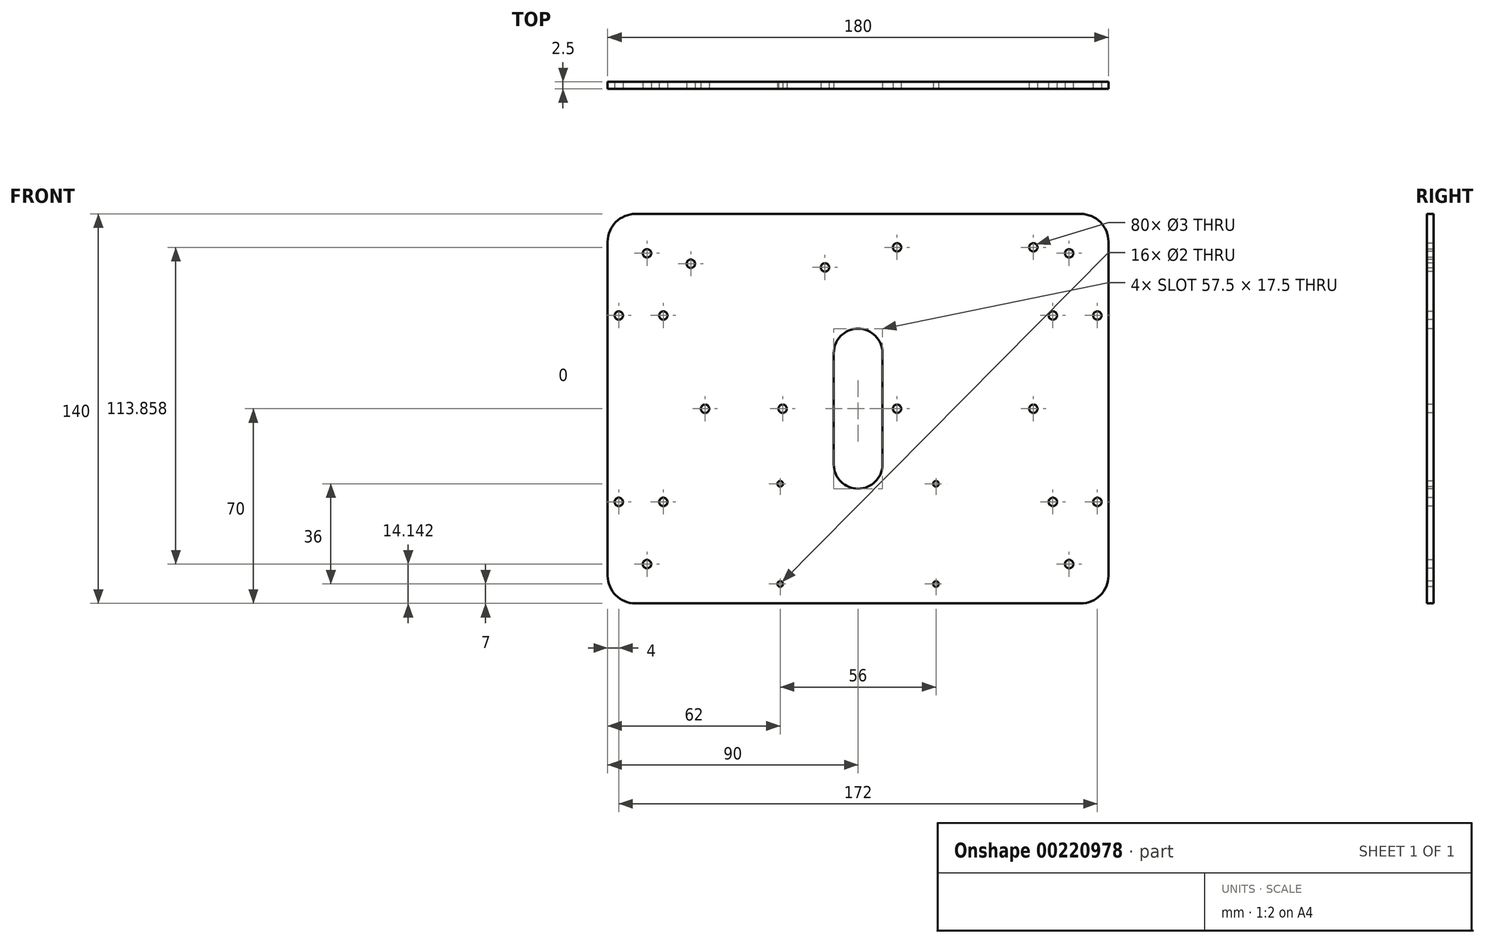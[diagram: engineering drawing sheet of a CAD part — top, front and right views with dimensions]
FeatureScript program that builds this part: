
annotation { "Feature Type Name" : "Feature", "Feature Type Description" : "" }
export const myFeature = defineFeature(function(context is Context, id is Id, definition is map)
    precondition{}
    {
        {
            var Q0;
            Q0=qCreatedBy(makeId("Front.planeOp"),FACE);
            var sketch = newSketch(context, id + "F0", { "sketchPlane" : qUnion([Q0])});
            skLineSegment(sketch, "E0.bottom", {"start": v(90, 70) * mm, "end": v(-90, 70) * mm});
            skLineSegment(sketch, "E0.top", {"start": v(90, -70) * mm, "end": v(-90, -70) * mm});
            skLineSegment(sketch, "E0.left", {"start": v(90, 70) * mm, "end": v(90, -70) * mm});
            skLineSegment(sketch, "E0.right", {"start": v(-90, 70) * mm, "end": v(-90, -70) * mm});
            skPoint(sketch, "E0.middle", {"position": v(0, 0) * mm});
            skSolve(sketch);
        }
        {
            var Q0;
            Q0 = qSketchRegion(id + "F0", true);
            extrude(context, id + "F1", {"entities" : qUnion([Q0]), "depth" : 2.5 * mm});
        }
        {
            var Q0;
            Q0=makeQuery(id+"F1.opExtrude","CAP_FACE",FACE,{"disambiguationData":[OSD([sQuery(id+"F0.wireOp",EDGE,"E0.bottom"),sQuery(id+"F0.wireOp",EDGE,"E0.top"),sQuery(id+"F0.wireOp",EDGE,"E0.left"),sQuery(id+"F0.wireOp",EDGE,"E0.right")])],"isStart":false});
            var sketch = newSketch(context, id + "F2", { "sketchPlane" : qUnion([Q0])});
            skCircle(sketch, "E1", {"center": v(75.86, 55.86) * mm, "radius": 1.5 * mm});
            skCircle(sketch, "E2.MirrorC", {"center": v(-75.86, 55.86) * mm, "radius": 1.5 * mm});
            skCircle(sketch, "E3.MirrorC", {"center": v(75.86, -55.86) * mm, "radius": 1.5 * mm});
            skCircle(sketch, "E4.MirrorC", {"center": v(-75.86, -55.86) * mm, "radius": 1.5 * mm});
            skLineSegment(sketch, "E5", {"start": v(-8.75, 0) * mm, "end": v(-8.75, 20) * mm});
            skLineSegment(sketch, "E6", {"start": v(8.75, 0) * mm, "end": v(8.75, 20) * mm});
            skArc(sketch, "E7", {"start": v(-8.75, 20) * mm, "mid": v(0, 28.75) * mm, "end": v(8.75, 20) * mm});
            skLineSegment(sketch, "E8.MirrorCS", {"start": v(-8.75, 0) * mm, "end": v(-8.75, -20) * mm});
            skArc(sketch, "E9.MirrorCS", {"start": v(-8.75, -20) * mm, "mid": v(0, -28.75) * mm, "end": v(8.75, -20) * mm});
            skLineSegment(sketch, "E10.MirrorCS", {"start": v(8.75, 0) * mm, "end": v(8.75, -20) * mm});
            skLineSegment(sketch, "E11", {"start": v(-90, 0) * mm, "end": v(-55, 0) * mm});
            skCircle(sketch, "E12", {"center": v(-55, 0) * mm, "radius": 1.5 * mm});
            skLineSegment(sketch, "E13", {"start": v(-55, 0) * mm, "end": v(-55, 52.1) * mm});
            skLineSegment(sketch, "E14", {"start": v(-55, 52.1) * mm, "end": v(-60.1, 52.1) * mm});
            skCircle(sketch, "E15", {"center": v(-60.1, 52.1) * mm, "radius": 1.5 * mm});
            skLineSegment(sketch, "E16", {"start": v(-55, 52.1) * mm, "end": v(-11.9, 52.1) * mm});
            skLineSegment(sketch, "E17", {"start": v(-11.9, 52.1) * mm, "end": v(-11.9, 50.8) * mm});
            skCircle(sketch, "E18", {"center": v(-11.9, 50.8) * mm, "radius": 1.5 * mm});
            skLineSegment(sketch, "E19", {"start": v(90, 0) * mm, "end": v(63, 0) * mm});
            skPoint(sketch, "E19.endSnap0", {"position": v(90, 0) * mm});
            skCircle(sketch, "E20", {"center": v(63, 0) * mm, "radius": 1.5 * mm});
            skLineSegment(sketch, "E21", {"start": v(63, 0) * mm, "end": v(63, 58) * mm});
            skLineSegment(sketch, "E22", {"start": v(63, 58) * mm, "end": v(14, 58) * mm});
            skLineSegment(sketch, "E23", {"start": v(14, 58) * mm, "end": v(14, 0) * mm});
            skCircle(sketch, "E24", {"center": v(14, 0) * mm, "radius": 1.5 * mm});
            skCircle(sketch, "E25", {"center": v(14, 58) * mm, "radius": 1.5 * mm});
            skCircle(sketch, "E26", {"center": v(63, 58) * mm, "radius": 1.5 * mm});
            skLineSegment(sketch, "E27", {"start": v(-55, 0) * mm, "end": v(-27.1, 0) * mm});
            skCircle(sketch, "E28", {"center": v(-27.1, 0) * mm, "radius": 1.5 * mm});
            skLineSegment(sketch, "E29.bottom", {"start": v(30, -65) * mm, "end": v(-30, -65) * mm});
            skPoint(sketch, "E29.middle", {"position": v(0, -45) * mm});
            skLineSegment(sketch, "E30", {"start": v(0, -70) * mm, "end": v(0, -65) * mm});
            skLineSegment(sketch, "E31", {"start": v(-30, -65) * mm, "end": v(-28, -65) * mm});
            skLineSegment(sketch, "E32", {"start": v(-28, -65) * mm, "end": v(-28, -63) * mm});
            skLineSegment(sketch, "E33", {"start": v(-28, -63) * mm, "end": v(-28, -27) * mm});
            skLineSegment(sketch, "E34", {"start": v(-28, -27) * mm, "end": v(28, -27) * mm});
            skLineSegment(sketch, "E35", {"start": v(28, -27) * mm, "end": v(28, -63) * mm});
            skCircle(sketch, "E36", {"center": v(-28, -27) * mm, "radius": 1 * mm});
            skCircle(sketch, "E37", {"center": v(28, -27) * mm, "radius": 1 * mm});
            skCircle(sketch, "E38", {"center": v(-28, -63) * mm, "radius": 1 * mm});
            skCircle(sketch, "E39", {"center": v(28, -63) * mm, "radius": 1 * mm});
            skLineSegment(sketch, "E40", {"start": v(90, 0) * mm, "end": v(78, 0) * mm});
            skLineSegment(sketch, "E41", {"start": v(78, 0) * mm, "end": v(78, 33.5) * mm});
            skLineSegment(sketch, "E42", {"start": v(78, 0) * mm, "end": v(78, -33.5) * mm});
            skLineSegment(sketch, "E43", {"start": v(78, -33.5) * mm, "end": v(70, -33.5) * mm});
            skLineSegment(sketch, "E44", {"start": v(78, -33.5) * mm, "end": v(86, -33.5) * mm});
            skLineSegment(sketch, "E45", {"start": v(78, 33.5) * mm, "end": v(86, 33.5) * mm});
            skLineSegment(sketch, "E46", {"start": v(78, 33.5) * mm, "end": v(70, 33.5) * mm});
            skLineSegment(sketch, "E47", {"start": v(-90, 0) * mm, "end": v(-78, 0) * mm});
            skLineSegment(sketch, "E48", {"start": v(-78, 0) * mm, "end": v(-78, 33.5) * mm});
            skLineSegment(sketch, "E49", {"start": v(-78, 0) * mm, "end": v(-78, -33.5) * mm});
            skLineSegment(sketch, "E50", {"start": v(-78, -33.5) * mm, "end": v(-70, -33.5) * mm});
            skLineSegment(sketch, "E51", {"start": v(-78, -33.5) * mm, "end": v(-86, -33.5) * mm});
            skLineSegment(sketch, "E52", {"start": v(-78, 33.5) * mm, "end": v(-70, 33.5) * mm});
            skLineSegment(sketch, "E53", {"start": v(-78, 33.5) * mm, "end": v(-86, 33.5) * mm});
            skCircle(sketch, "E54", {"center": v(-86, 33.5) * mm, "radius": 1.5 * mm});
            skCircle(sketch, "E55", {"center": v(-70, 33.5) * mm, "radius": 1.5 * mm});
            skCircle(sketch, "E56", {"center": v(-86, -33.5) * mm, "radius": 1.5 * mm});
            skCircle(sketch, "E57", {"center": v(-70, -33.5) * mm, "radius": 1.5 * mm});
            skCircle(sketch, "E58", {"center": v(70, -33.5) * mm, "radius": 1.5 * mm});
            skCircle(sketch, "E59", {"center": v(86, -33.5) * mm, "radius": 1.5 * mm});
            skCircle(sketch, "E60", {"center": v(70, 33.5) * mm, "radius": 1.5 * mm});
            skCircle(sketch, "E61", {"center": v(86, 33.5) * mm, "radius": 1.5 * mm});
            skSolve(sketch);
        }
        {
            var Q0;
            Q0 = qSketchRegion(id + "F2", true);
            extrude(context, id + "F3", {"entities" : qUnion([Q0]), "operationType" : NewBodyOperationType.REMOVE, "oppositeDirection" : true, "depth" : 5 * mm});
        }
        {
            var Q0;
            Q0=makeQuery(id+"F1.opExtrude","SWEPT_EDGE",EDGE,{"disambiguationData":[OSD([sQuery(id+"F0.wireOp",EDGE,"E0.bottom"),sQuery(id+"F0.wireOp",EDGE,"E0.right")])]});
            var Q1;
            Q1=makeQuery(id+"F1.opExtrude","SWEPT_EDGE",EDGE,{"disambiguationData":[OSD([sQuery(id+"F0.wireOp",EDGE,"E0.top"),sQuery(id+"F0.wireOp",EDGE,"E0.right")])]});
            var Q2;
            Q2=makeQuery(id+"F1.opExtrude","SWEPT_EDGE",EDGE,{"disambiguationData":[OSD([sQuery(id+"F0.wireOp",EDGE,"E0.top"),sQuery(id+"F0.wireOp",EDGE,"E0.left")])]});
            var Q3;
            Q3=makeQuery(id+"F1.opExtrude","SWEPT_EDGE",EDGE,{"disambiguationData":[OSD([sQuery(id+"F0.wireOp",EDGE,"E0.bottom"),sQuery(id+"F0.wireOp",EDGE,"E0.left")])]});
            fillet(context, id + "F4", {"entities" : qUnion([Q0, Q1, Q2, Q3]), "radius" : 10 * mm, "tangentPropagation" : true, "allowEdgeOverflow" : false});
        }
    });
